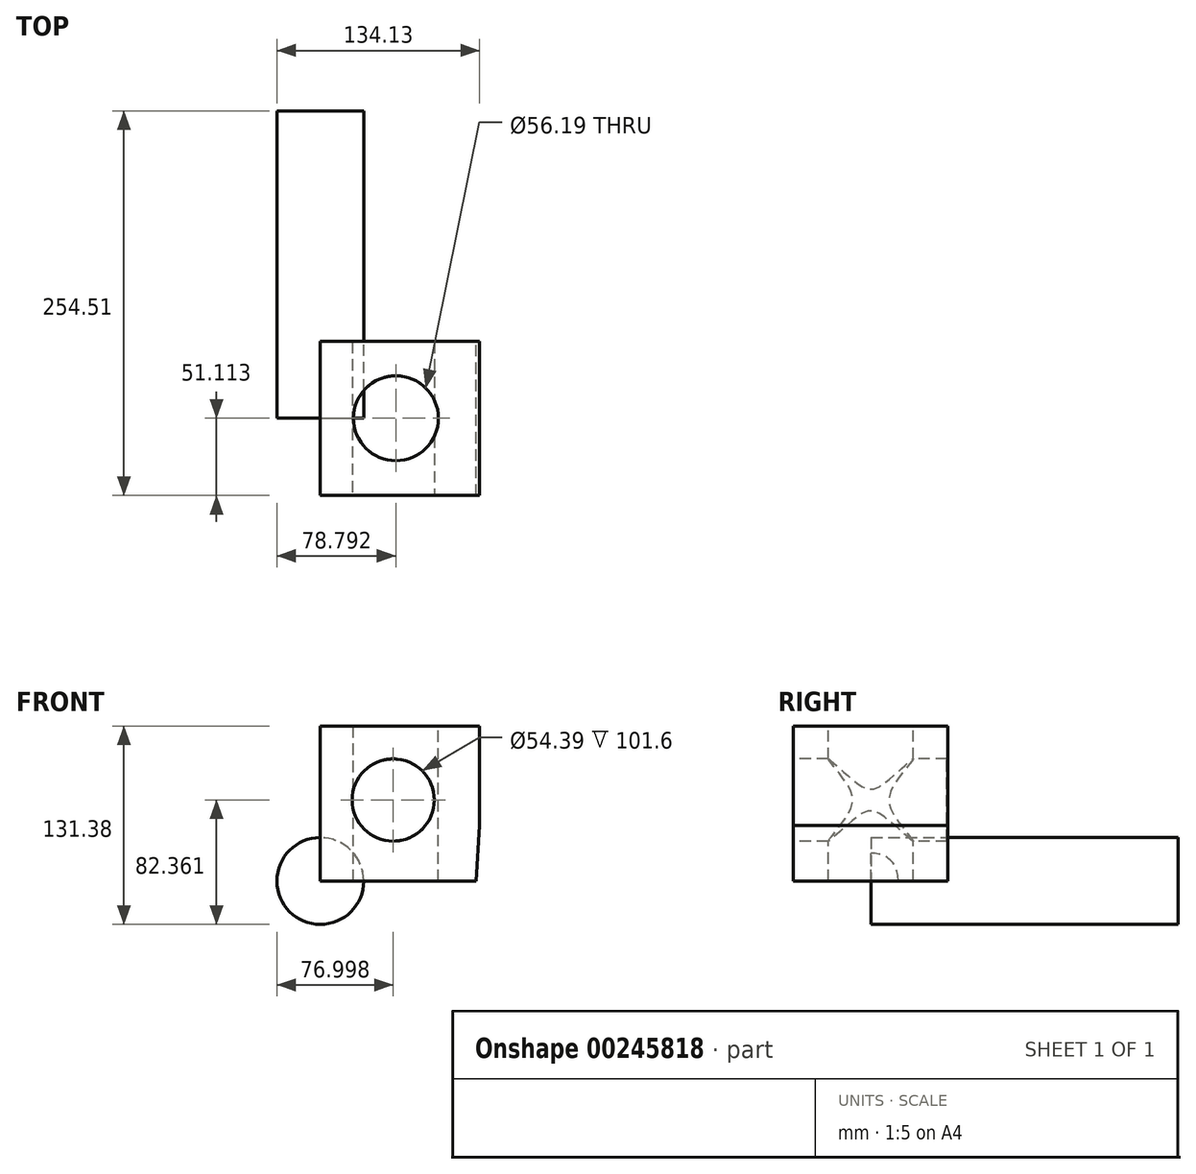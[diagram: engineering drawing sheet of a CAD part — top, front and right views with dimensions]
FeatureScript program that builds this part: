
annotation { "Feature Type Name" : "Feature", "Feature Type Description" : "" }
export const myFeature = defineFeature(function(context is Context, id is Id, definition is map)
    precondition{}
    {
        {
            var Q0;
            Q0=qCreatedBy(makeId("Front.planeOp"),FACE);
            var sketch = newSketch(context, id + "F0", { "sketchPlane" : qUnion([Q0])});
            skLineSegment(sketch, "E0", {"start": v(0, 0) * mm, "end": v(99.56, 0) * mm});
            skLineSegment(sketch, "E1", {"start": v(99.56, 0) * mm, "end": v(0, 0) * mm});
            skLineSegment(sketch, "E2", {"start": v(0, 0) * mm, "end": v(103, 0) * mm});
            skLineSegment(sketch, "E3", {"start": v(103, 0) * mm, "end": v(105.4, 36.74) * mm});
            skLineSegment(sketch, "E4", {"start": v(105.4, 36.74) * mm, "end": v(105.4, 48.4) * mm});
            skLineSegment(sketch, "E5", {"start": v(105.4, 48.4) * mm, "end": v(105.4, 63.51) * mm});
            skLineSegment(sketch, "E6", {"start": v(105.4, 63.51) * mm, "end": v(105.4, 102.65) * mm});
            skLineSegment(sketch, "E7", {"start": v(105.4, 102.65) * mm, "end": v(0, 102.65) * mm});
            skLineSegment(sketch, "E8", {"start": v(0, 102.65) * mm, "end": v(0, 0) * mm});
            skSolve(sketch);
        }
        {
            var Q0;
            {var subQ0=sQuery(id+"F0.wireOp",EDGE,"E3");Q0=makeQuery(id+"F0.imprint","IMPRINT",FACE,{"disambiguationData":[TD([[makeQuery(id+"F0.imprint","IMPRINT",EDGE,{"derivedFrom":subQ0}),1.0]])]});}
            extrude(context, id + "F1", {"entities" : qUnion([Q0]), "depth" : 102.1 * mm});
        }
        {
            var Q0;
            Q0=makeQuery(id+"F1.opExtrude","SWEPT_FACE",FACE,{"disambiguationData":[OSD([sQuery(id+"F0.wireOp",EDGE,"E7")])]});
            var sketch = newSketch(context, id + "F2", { "sketchPlane" : qUnion([Q0])});
            skCircle(sketch, "E9", {"center": v(50.06, -51) * mm, "radius": 28.1 * mm});
            skSolve(sketch);
        }
        {
            var Q0;
            Q0=makeQuery(id+"F2.imprint","IMPRINT",FACE,{"disambiguationData":[TD([[makeQuery(id+"F2.imprint","IMPRINT",EDGE,{"derivedFrom":sQuery(id+"F2.wireOp",EDGE,"E9")}),1.0]])]});
            extrude(context, id + "F3", {"entities" : qUnion([Q0]), "operationType" : NewBodyOperationType.REMOVE, "oppositeDirection" : true, "depth" : 101.6 * mm});
        }
        {
            var Q0;
            Q0=makeQuery(id+"F3.boolean.opBoolean","COPY",FACE,{"derivedFrom":makeQuery(id+"F3.opExtrude","CAP_FACE",FACE,{"disambiguationData":[OSD([sQuery(id+"F2.wireOp",EDGE,"E9")])],"isStart":false})});
            extrude(context, id + "F4", {"entities" : qUnion([Q0]), "operationType" : NewBodyOperationType.REMOVE, "oppositeDirection" : true, "depth" : 101.6 * mm});
        }
        {
            var Q0;
            Q0=makeQuery(id+"F1.opExtrude","CAP_FACE",FACE,{"disambiguationData":[OSD([sQuery(id+"F0.wireOp",EDGE,"E2"),sQuery(id+"F0.wireOp",EDGE,"E3"),sQuery(id+"F0.wireOp",EDGE,"E4"),sQuery(id+"F0.wireOp",EDGE,"E5"),sQuery(id+"F0.wireOp",EDGE,"E6"),sQuery(id+"F0.wireOp",EDGE,"E7"),sQuery(id+"F0.wireOp",EDGE,"E8")])],"isStart":false});
            var sketch = newSketch(context, id + "F5", { "sketchPlane" : qUnion([Q0])});
            skCircle(sketch, "E10", {"center": v(48.27, 53.63) * mm, "radius": 27.2 * mm});
            skSolve(sketch);
        }
        {
            var Q0;
            Q0 = qSketchRegion(id + "F5", true);
            extrude(context, id + "F6", {"entities" : qUnion([Q0]), "operationType" : NewBodyOperationType.REMOVE, "oppositeDirection" : true, "depth" : 101.6 * mm});
        }
        {
            var Q0;
            Q0=qCreatedBy(makeId("Front.planeOp"),FACE);
            var sketch = newSketch(context, id + "F7", { "sketchPlane" : qUnion([Q0])});
            skCircle(sketch, "E11", {"center": v(0, 0) * mm, "radius": 28.73 * mm});
            skSolve(sketch);
        }
        {
            var Q0;
            Q0=makeQuery(id+"F7.imprint","IMPRINT",FACE,{"disambiguationData":[TD([[makeQuery(id+"F7.imprint","IMPRINT",EDGE,{"derivedFrom":sQuery(id+"F7.wireOp",EDGE,"E11")}),1.0]])]});
            extrude(context, id + "F8", {"entities" : qUnion([Q0]), "operationType" : NewBodyOperationType.ADD, "depth" : 50.8 * mm, "hasSecondDirection" : true, "secondDirectionOppositeDirection" : true, "secondDirectionDepth" : 152.4 * mm});
        }
    });
